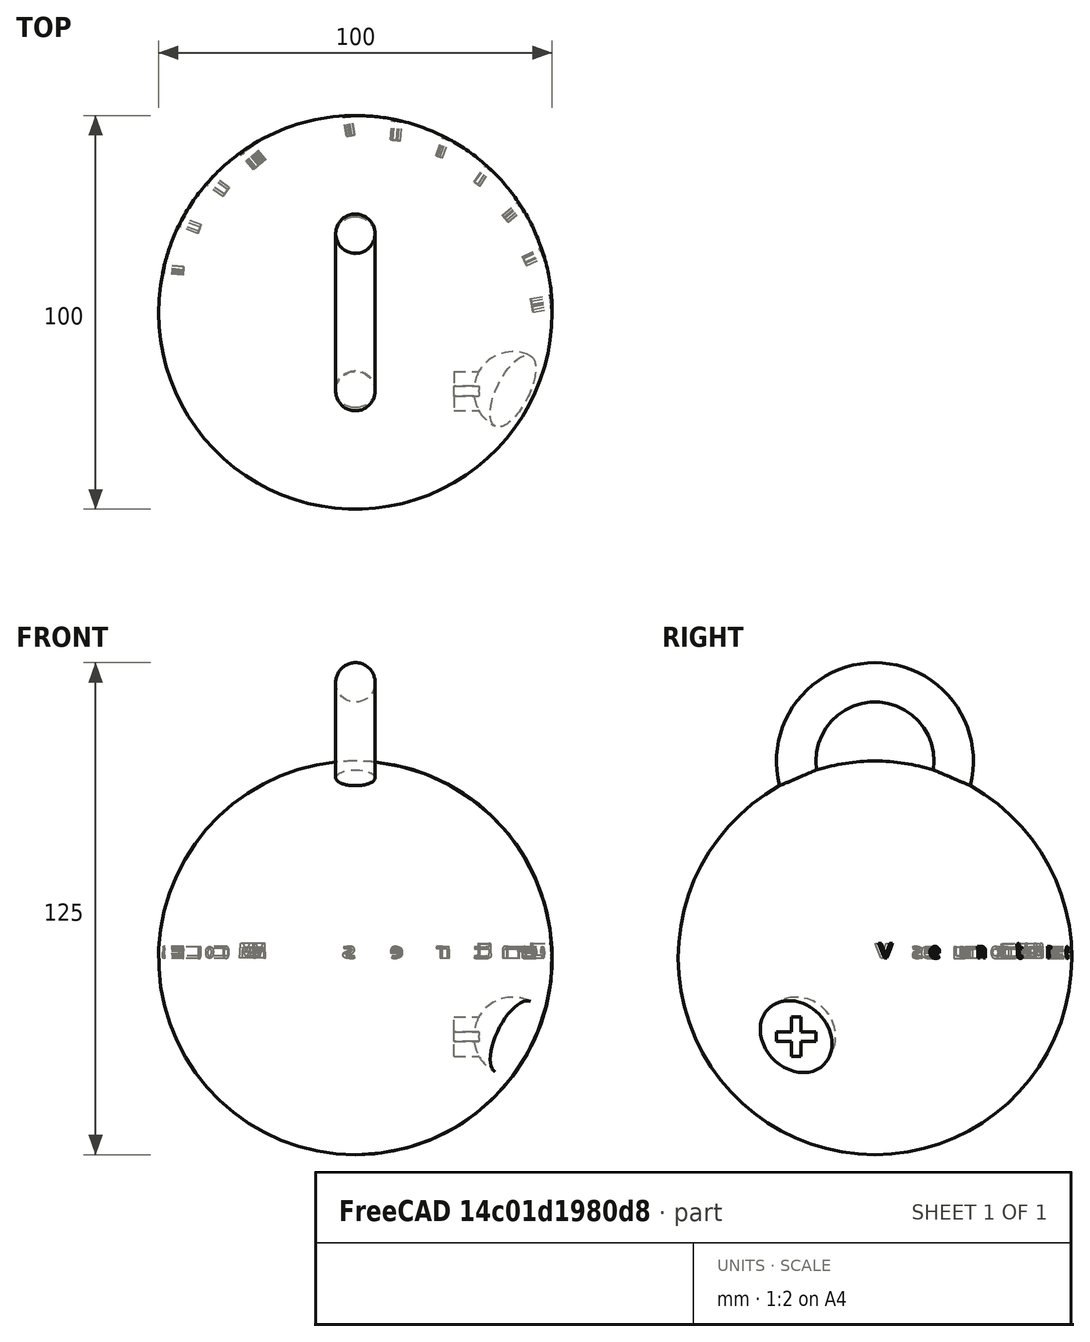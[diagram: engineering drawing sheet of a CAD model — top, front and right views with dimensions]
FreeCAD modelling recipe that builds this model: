
FCSTD DOCUMENT  (FreeCAD 0.16R6703 (Git))
Label: portecleventremoucreuxetinsciption
License: All rights reserved
LicenseURL: http://en.wikipedia.org/wiki/All_rights_reserved
objects: Part::Cut×15, Part::Part2DObjectPython×12, Part::Extrusion×12, Part::Sphere×2, Part::Box×2, Part::Torus×1, Part::MultiFuse×1, App::DocumentObjectGroup×1
note: 45 computed .brp shape members not serialized (recipe doc carries the construction recipe); baked Part::Feature solids carry a one-line shape summary decoded from their .brp

FEATURE [Part::Sphere] Sphere  label="Sphère"
  Angle1 = -90
  Angle2 = 90
  Angle3 = 360
  Radius = 50
FEATURE [Part::Sphere] Sphere001  label="Sphère001"
  Angle1 = -90
  Angle2 = 90
  Angle3 = 360
  Placement = pos=(40,-20,-20) rot=(0,0,1;0rad)
  Radius = 10
FEATURE [Part::Box] Box  label="Boîte"
  Height = 10
  Length = 10
  Placement = pos=(25,-21.25,-25) rot=(0,0,1;0rad)
  Width = 2.5
FEATURE [Part::Box] Box001  label="Boîte001"
  Height = 10
  Length = 10
  Placement = pos=(25,-15,-21.25) rot=(1,0,0;1.5708rad)
  Width = 2.5
FEATURE [Part::Torus] Torus  label="Tore"
  Angle1 = -180
  Angle2 = 180
  Angle3 = 360
  Placement = pos=(0,0,50) rot=(0,1,0;1.5708rad)
  Radius1 = 20
  Radius2 = 5
FEATURE [Part::Cut] Cut
  Base = -> Sphere
  Tool = -> Sphere001
FEATURE [Part::MultiFuse] Fusion
  Shapes = -> [Cut,Torus]
FEATURE [Part::Cut] Cut001
  Base = -> Fusion
  Tool = -> Box001
FEATURE [Part::Cut] Cut002
  Base = -> Cut001
  Tool = -> Box
FEATURE [Part::Part2DObjectPython] ShapeString  # Draft 2D object (typed FeaturePython)
  FontFile = <path>
  Size = 2
  String = V
  Tracking = 0
FEATURE [Part::Extrusion] Extrusion
  Base = -> ShapeString
  Dir = (0,0,10)
  Placement = pos=(45.15,0,0) rot=(0.510274,0.60812,0.60812;2.19793rad)
  Solid = false
FEATURE [Part::Part2DObjectPython] ShapeString001  # Draft 2D object (typed FeaturePython)
  FontFile = <path>
  Size = 2
  String = e
  Tracking = 0
FEATURE [Part::Extrusion] Extrusion001
  Base = -> ShapeString001
  Dir = (0,0,10)
  Placement = pos=(43.6116,11.6857,0) rot=(0.410726,0.644711,0.644711;2.36216rad)
  Solid = false
FEATURE [Part::Part2DObjectPython] ShapeString002  # Draft 2D object (typed FeaturePython)
  FontFile = <path>
  Size = 2
  String = n
  Tracking = 0
FEATURE [Part::Extrusion] Extrusion002
  Base = -> ShapeString002
  Dir = (0,0,10)
  Placement = pos=(39.101,22.575,0) rot=(0.313146,0.671543,0.671543;2.53465rad)
  Solid = false
FEATURE [Part::Part2DObjectPython] ShapeString003  # Draft 2D object (typed FeaturePython)
  FontFile = <path>
  Size = 2
  String = t
  Tracking = 0
FEATURE [Part::Extrusion] Extrusion003
  Base = -> ShapeString003
  Dir = (0,0,10)
  Placement = pos=(31.9259,31.9259,0) rot=(0.217607,0.690162,0.690162;2.71306rad)
  Solid = false
FEATURE [Part::Part2DObjectPython] ShapeString004  # Draft 2D object (typed FeaturePython)
  FontFile = <path>
  Size = 2
  String = r
  Tracking = 0
FEATURE [Part::Extrusion] Extrusion004
  Base = -> ShapeString004
  Dir = (0,0,10)
  Placement = pos=(22.575,39.101,0) rot=(0.123724,0.701674,0.701674;2.8954rad)
  Solid = false
FEATURE [Part::Part2DObjectPython] ShapeString005  # Draft 2D object (typed FeaturePython)
  FontFile = <path>
  Size = 2
  String = e
  Tracking = 0
FEATURE [Part::Extrusion] Extrusion005
  Base = -> ShapeString005
  Dir = (0,0,10)
  Placement = pos=(11.6857,43.6116,0) rot=(0.030858,0.70677,0.70677;3.0799rad)
  Solid = false
FEATURE [Part::Part2DObjectPython] ShapeString006  # Draft 2D object (typed FeaturePython)
  FontFile = <path>
  Size = 2
  String = s
  Tracking = 0
FEATURE [Part::Extrusion] Extrusion006
  Base = -> ShapeString006
  Dir = (0,0,10)
  Placement = pos=(0,45.15,0) rot=(-0.061746,0.705758,0.705758;3.26493rad)
  Solid = false
FEATURE [Part::Part2DObjectPython] ShapeString007  # Draft 2D object (typed FeaturePython)
  FontFile = <path>
  Size = 2
  Tracking = 0
FEATURE [Part::Extrusion] Extrusion007
  Base = -> ShapeString007
  Dir = (0,0,10)
  Placement = pos=(-11.6857,43.6116,0) rot=(-0.15487,0.698575,0.698575;3.44889rad)
  Solid = false
FEATURE [Part::Part2DObjectPython] ShapeString008  # Draft 2D object (typed FeaturePython)
  FontFile = <path>
  Size = 2
  String = M
  Tracking = 0
FEATURE [Part::Extrusion] Extrusion008
  Base = -> ShapeString008
  Dir = (0,0,10)
  Placement = pos=(-22.575,39.101,0) rot=(-0.249244,0.684791,0.684791;3.63013rad)
  Solid = false
FEATURE [Part::Part2DObjectPython] ShapeString009  # Draft 2D object (typed FeaturePython)
  FontFile = <path>
  Size = 2
  String = o
  Tracking = 0
FEATURE [Part::Extrusion] Extrusion009
  Base = -> ShapeString009
  Dir = (0,0,10)
  Placement = pos=(-31.9259,31.9259,0) rot=(-0.345437,0.663579,0.663579;3.8068rad)
  Solid = false
FEATURE [Part::Part2DObjectPython] ShapeString010  # Draft 2D object (typed FeaturePython)
  FontFile = <path>
  Size = 2
  String = u
  Tracking = 0
FEATURE [Part::Extrusion] Extrusion010
  Base = -> ShapeString010
  Dir = (0,0,10)
  Placement = pos=(-39.101,22.575,0) rot=(-0.443713,0.633687,0.633687;3.97682rad)
  Solid = false
FEATURE [Part::Part2DObjectPython] ShapeString011  # Draft 2D object (typed FeaturePython)
  FontFile = <path>
  Size = 2
  String = s
  Tracking = 0
FEATURE [Part::Extrusion] Extrusion011
  Base = -> ShapeString011
  Dir = (0,0,10)
  Placement = pos=(-43.6116,11.6857,0) rot=(-0.543775,0.593426,0.593426;4.13769rad)
  Solid = false
FEATURE [Part::Cut] Cut003
  Base = -> Cut002
  Tool = -> Extrusion
FEATURE [Part::Cut] Cut004
  Base = -> Cut003
  Tool = -> Extrusion011
FEATURE [Part::Cut] Cut005
  Base = -> Cut004
  Tool = -> Extrusion010
FEATURE [Part::Cut] Cut006
  Base = -> Cut005
  Tool = -> Extrusion009
FEATURE [Part::Cut] Cut007
  Base = -> Cut006
  Tool = -> Extrusion008
FEATURE [Part::Cut] Cut008
  Base = -> Cut007
  Tool = -> Extrusion007
FEATURE [Part::Cut] Cut009
  Base = -> Cut008
  Tool = -> Extrusion006
FEATURE [Part::Cut] Cut010
  Base = -> Cut009
  Tool = -> Extrusion005
FEATURE [Part::Cut] Cut011
  Base = -> Cut010
  Tool = -> Extrusion004
FEATURE [Part::Cut] Cut012
  Base = -> Cut011
  Tool = -> Extrusion003
FEATURE [Part::Cut] Cut013
  Base = -> Cut012
  Tool = -> Extrusion002
FEATURE [Part::Cut] Cut014
  Base = -> Cut013
  Tool = -> Extrusion001
FEATURE [App::DocumentObjectGroup] FcString
  Group = -> [ShapeString,ShapeString001,ShapeString002,ShapeString003,ShapeString004,ShapeString005,ShapeString006,ShapeString007,ShapeString008,ShapeString009,ShapeString010,ShapeString011,Cut014]
note: 12 file-system paths scrubbed to <path> (originals preserved in the JSON sidecar)
